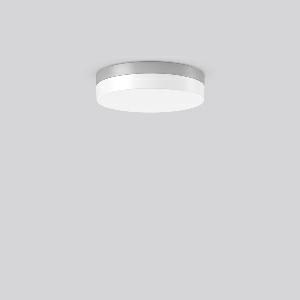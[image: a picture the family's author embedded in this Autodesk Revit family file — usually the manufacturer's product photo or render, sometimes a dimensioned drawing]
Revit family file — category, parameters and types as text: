
# Revit family: flat_slim_round_312674_004_1_19_4d80
name_source: partatom
category: Lighting Fixtures
units: mm (PartAtom-declared; Revit-internal decimal feet)

## family parameters
Cut with Voids When Loaded = No
Host = Face
Light Source = No
Part Type = Normal
Room Calculation Point = No
Round Connector Dimension = Use Diameter
Shared = No

## types (1)
- MultiLumen 1 830 (1 x LED Modul 830, 1450 lm, 3000)
    Apparent Load = 11 VA
    CIE Flux Codes = 38 68 88 84 100
    Color Rendering = 80
    Color Temperature = 3000
    Default Elevation = 1800 mm
    Height = 70 mm
    Lamp = 1 x LED Modul 830
    Lamp Light Flux = 1450 lm
    Lamp count = 1
    Length = 300 mm
    Lifetime = 50000 h
    Luminous efficacy = 132 lm/W
    Manufacturer = RZB
    ModVariant = No
    Model = 312674.004.1.19
    Mounting Place = Ceiling
    Mounting Type = Surface mounted
    Number of Poles = 1
    OnlyDefault = Yes
    Power Factor = 1
    Product Name = FLAT SLIM round
    Product group = Surface mounted ceiling and wall luminaires
    ProductGroupID = 305
    Protection Class = Protection class I
    Protection Degree = Degree of protection
    RLX_Detail_Level = 1
    RLX_Emergency_Light_Flux = 0 lm
    RLX_Emergency_Type = 0
    RLX_Emergency_Type_DB = No
    RlxData = <blob elided: 17281 chars, md5=44bef7a4>
    Socket = socket
    Standby Power = 0 W
    System Light Flux = 1450 lm
    System Power = 11 W
    Type Comments = MultiLumen 1 830
    Type Image = 312629.004.jpg
    URL = http://relux.com
    VarID = multilumen_1_830
    Voltage = 0 V
    Weight = 0.00 kg
    Width = 0 mm  [stored 0 ft]

note: [stored X ft] marks values corroborated as IEEE doubles in the binary element streams (Revit-internal decimal feet)

## geometry (parser evidence)
native form markers: Blend x4, Sweep x12
no freeform markers — native parametric forms only
